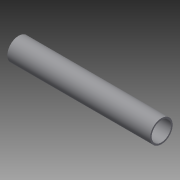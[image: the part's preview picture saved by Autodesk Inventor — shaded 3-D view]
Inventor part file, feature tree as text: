
AUTODESK INVENTOR PART (.ipt)
format: ipt  version: 2015 SP1 (Build 190203100, 203)  size: 74,752 bytes
history: native  units: in
note: dims shown in document units (in); Inventor stores cm internally (conversion verified against a paired STEP export)
features: extrude x1, sketch x1
ambient origin geometry x8: Origin, YZ Plane, XZ Plane, XY Plane, X Axis, Y Axis, Z Axis, Center Point
bodies: Solid1 (feature_tree)
feature tree (2):
  extrude  "Extrusion1"  Depth=15.0in
  sketch  "Sketch1"  dims[d0=2.047in d1=2.375in d2=15.0in d3=0.0in]
